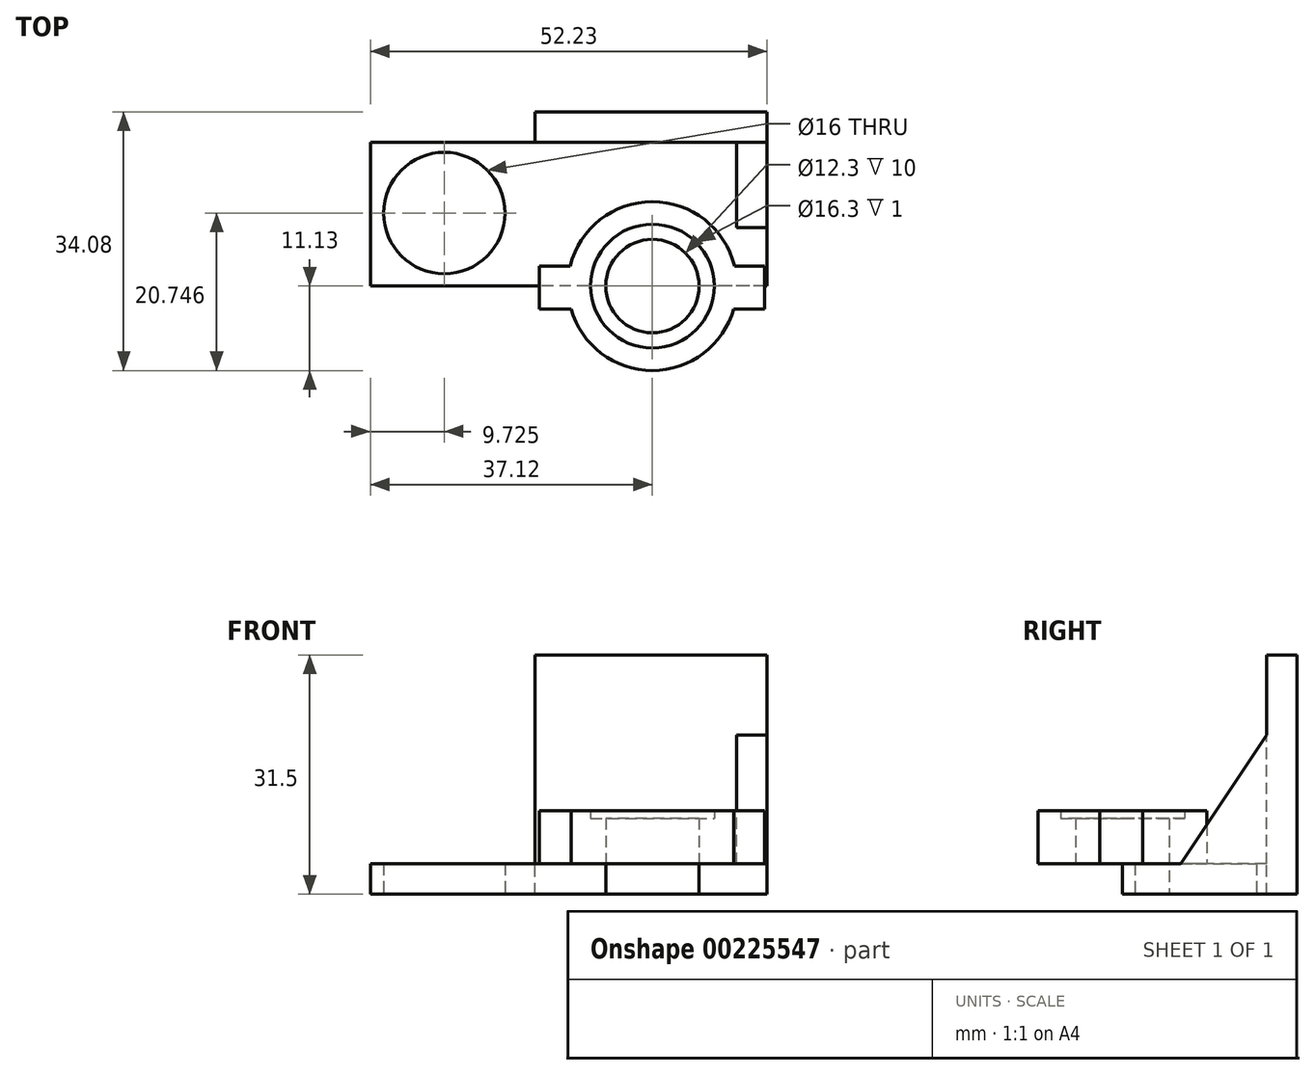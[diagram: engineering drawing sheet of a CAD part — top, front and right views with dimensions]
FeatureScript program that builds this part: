
annotation { "Feature Type Name" : "Feature", "Feature Type Description" : "" }
export const myFeature = defineFeature(function(context is Context, id is Id, definition is map)
    precondition{}
    {
        {
            var Q0;
            Q0=qCreatedBy(makeId("Top.planeOp"),FACE);
            var sketch = newSketch(context, id + "F0", { "sketchPlane" : qUnion([Q0])});
            skLineSegment(sketch, "E0.bottom", {"start": v(15.1, 0) * mm, "end": v(-37.12, 0) * mm});
            skLineSegment(sketch, "E0.top", {"start": v(15.1, 18.95) * mm, "end": v(-37.12, 18.95) * mm});
            skLineSegment(sketch, "E0.left", {"start": v(15.1, 18.95) * mm, "end": v(15.1, 0) * mm});
            skLineSegment(sketch, "E0.right", {"start": v(-37.12, 18.95) * mm, "end": v(-37.12, 0) * mm});
            skPoint(sketch, "E1", {"position": v(-27.4, 9.62) * mm});
            skSolve(sketch);
        }
        {
            var Q0;
            Q0 = qSketchRegion(id + "F0", true);
            extrude(context, id + "F1", {"entities" : qUnion([Q0]), "depth" : 4 * mm});
        }
        {
            var Q0;
            Q0=sQuery(id+"F0.wireOp",VERTEX,"E1");
            var Q1;
            Q1=makeQuery(id+"F1.opExtrude","SWEPT_BODY",BODY,{"disambiguationData":[OSD([sQuery(id+"F0.wireOp",EDGE,"E0.bottom"),sQuery(id+"F0.wireOp",EDGE,"E0.top"),sQuery(id+"F0.wireOp",EDGE,"E0.left"),sQuery(id+"F0.wireOp",EDGE,"E0.right")])]});
            hole(context, id + "F2", {"style" : HoleStyle.SIMPLE, "endStyle" : HoleEndStyle.THROUGH, "oppositeDirection" : true, "holeDiameter" : 16 * mm, "locations" : qUnion([Q0]), "scope" : qUnion([Q1]), "isTappedThrough" : true});
        }
        {
            var Q0;
            Q0=makeQuery(id+"F1.opExtrude","CAP_FACE",FACE,{"disambiguationData":[OSD([sQuery(id+"F0.wireOp",EDGE,"E0.bottom"),sQuery(id+"F0.wireOp",EDGE,"E0.top"),sQuery(id+"F0.wireOp",EDGE,"E0.left"),sQuery(id+"F0.wireOp",EDGE,"E0.right")])],"isStart":false});
            var sketch = newSketch(context, id + "F3", { "sketchPlane" : qUnion([Q0])});
            skLineSegment(sketch, "E2.bottom", {"start": v(-14.86, 2.65) * mm, "end": v(-10.81, 2.65) * mm});
            skLineSegment(sketch, "E2.top", {"start": v(-14.86, -3) * mm, "end": v(-10.72, -3) * mm});
            skLineSegment(sketch, "E2.left", {"start": v(-14.86, 2.65) * mm, "end": v(-14.86, -3) * mm});
            skLineSegment(sketch, "E2.right", {"start": v(14.8, 2.65) * mm, "end": v(14.8, -3) * mm});
            skArc(sketch, "E3", {"start": v(10.81, 2.65) * mm, "mid": v(0, 11.13) * mm, "end": v(-10.81, 2.65) * mm});
            skArc(sketch, "E4", {"start": v(10.72, -3) * mm, "mid": v(11.13, -0.18) * mm, "end": v(10.81, 2.65) * mm});
            skLineSegment(sketch, "E5", {"start": v(-10.72, -3) * mm, "end": v(-10.72, -3) * mm});
            skArc(sketch, "E6", {"start": v(-10.81, 2.65) * mm, "mid": v(-2.83, -10.77) * mm, "end": v(10.72, -3) * mm});
            skLineSegment(sketch, "E7", {"start": v(10.81, 2.65) * mm, "end": v(14.8, 2.65) * mm});
            skLineSegment(sketch, "E8", {"start": v(10.72, -3) * mm, "end": v(14.8, -3) * mm});
            skSolve(sketch);
        }
        {
            var Q0;
            Q0 = qSketchRegion(id + "F3", true);
            extrude(context, id + "F4", {"entities" : qUnion([Q0]), "operationType" : NewBodyOperationType.ADD, "depth" : 7 * mm});
        }
        {
            var Q0;
            Q0=qCreatedBy(makeId("Top.planeOp"),FACE);
            var sketch = newSketch(context, id + "F5", { "sketchPlane" : qUnion([Q0])});
            skCircle(sketch, "E9", {"center": v(0, 0) * mm, "radius": 6.15 * mm});
            skSolve(sketch);
        }
        {
            var Q0;
            Q0 = qSketchRegion(id + "F5", true);
            extrude(context, id + "F6", {"entities" : qUnion([Q0]), "operationType" : NewBodyOperationType.REMOVE, "depth" : 10 * mm});
        }
        {
            var Q0;
            Q0=makeQuery(id+"F6.boolean.opBoolean","COPY",FACE,{"derivedFrom":makeQuery(id+"F6.opExtrude","CAP_FACE",FACE,{"disambiguationData":[OSD([sQuery(id+"F5.wireOp",EDGE,"E9")])],"isStart":false})});
            var sketch = newSketch(context, id + "F7", { "sketchPlane" : qUnion([Q0])});
            skCircle(sketch, "E10", {"center": v(0, 0) * mm, "radius": 8.15 * mm});
            skSolve(sketch);
        }
        {
            var Q0;
            Q0 = qSketchRegion(id + "F7", true);
            extrude(context, id + "F8", {"entities" : qUnion([Q0]), "operationType" : NewBodyOperationType.REMOVE, "oppositeDirection" : true, "depth" : 3.72 * mm});
        }
        {
            var Q0;
            Q0=makeQuery(id+"F1.opExtrude","SWEPT_FACE",FACE,{"disambiguationData":[OSD([sQuery(id+"F0.wireOp",EDGE,"E0.top")])]});
            var sketch = newSketch(context, id + "F9", { "sketchPlane" : qUnion([Q0])});
            skLineSegment(sketch, "E11.bottom", {"start": v(-15.1, 0) * mm, "end": v(15.48, 0) * mm});
            skLineSegment(sketch, "E11.top", {"start": v(-15.1, 31.5) * mm, "end": v(15.48, 31.5) * mm});
            skLineSegment(sketch, "E11.left", {"start": v(-15.1, 0) * mm, "end": v(-15.1, 31.5) * mm});
            skLineSegment(sketch, "E11.right", {"start": v(15.48, 0) * mm, "end": v(15.48, 31.5) * mm});
            skSolve(sketch);
        }
        {
            var Q0;
            Q0 = qSketchRegion(id + "F9", true);
            extrude(context, id + "F10", {"entities" : qUnion([Q0]), "operationType" : NewBodyOperationType.ADD, "depth" : 4 * mm});
        }
        {
            var Q0;
            Q0=makeQuery(id+"F10.boolean.opBoolean","MERGE",FACE,{"derivedFrom":[makeQuery(id+"F1.opExtrude","SWEPT_FACE",FACE,{"disambiguationData":[OSD([sQuery(id+"F0.wireOp",EDGE,"E0.left")])]}),makeQuery(id+"F10.opExtrude","SWEPT_FACE",FACE,{"disambiguationData":[OSD([sQuery(id+"F9.wireOp",EDGE,"E11.left")])]})]});
            var sketch = newSketch(context, id + "F11", { "sketchPlane" : qUnion([Q0])});
            skLineSegment(sketch, "E12", {"start": v(7.68, 4) * mm, "end": v(18.95, 20.96) * mm});
            skLineSegment(sketch, "E13", {"start": v(18.95, 20.96) * mm, "end": v(18.95, 4) * mm});
            skLineSegment(sketch, "E14", {"start": v(18.95, 4) * mm, "end": v(7.68, 4) * mm});
            skSolve(sketch);
        }
        {
            var Q0;
            Q0=makeQuery(id+"F11.imprint","IMPRINT",FACE,{"disambiguationData":[TD([[makeQuery(id+"F11.imprint","IMPRINT",EDGE,{"derivedFrom":sQuery(id+"F11.wireOp",EDGE,"E12")}),-1.0]])]});
            extrude(context, id + "F12", {"entities" : qUnion([Q0]), "operationType" : NewBodyOperationType.ADD, "oppositeDirection" : true, "depth" : 4 * mm});
        }
    });
